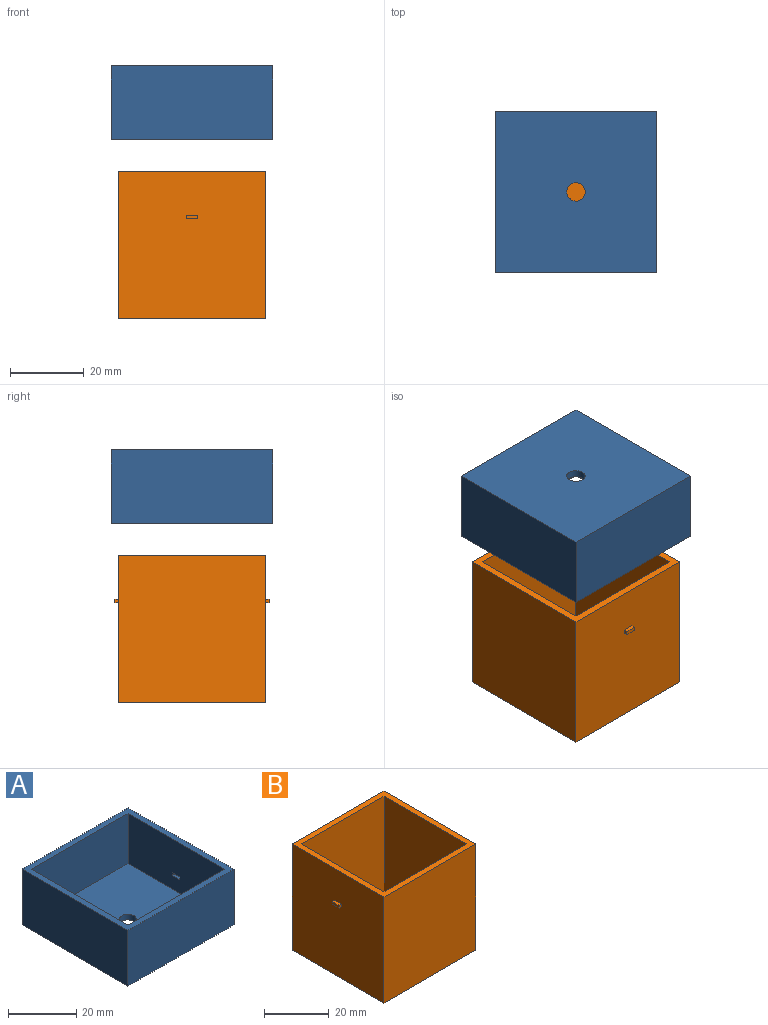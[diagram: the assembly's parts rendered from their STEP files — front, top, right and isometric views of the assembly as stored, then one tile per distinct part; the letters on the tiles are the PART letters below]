
ASSEMBLY  parts=2 mates=1
PART A: 22 faces, bbox 44x44x20 mm
  f0: plane 40x18mm, normal (1,0,0), area 717mm2, adj f2,f8,f9,f10,f17,f18,f19,f20
  f1: plane 40x18mm, normal (-1,0,0), area 717mm2, adj f2,f8,f9,f10,f12,f13,f14,f15
  f2: plane 44x44mm, normal (0,0,1), area 336mm2, adj f0,f1,f3,f4,f5,f6,f8,f9
  f3: plane 44x20mm, normal (0,1,0), area 880mm2, adj f2,f4,f6,f7
  f4: plane 44x20mm, normal (-1,0,0), area 880mm2, adj f2,f3,f5,f7
  f5: plane 44x20mm, normal (0,-1,0), area 880mm2, adj f2,f4,f6,f7
  f6: plane 44x20mm, normal (1,0,0), area 880mm2, adj f2,f3,f5,f7
  f7: plane 44x44mm, normal (0,0,-1), area 1916.4mm2, adj f3,f4,f5,f6,f11
  f8: plane 40x18mm, normal (0,-1,0), area 720mm2, adj f0,f1,f2,f10
  f9: plane 40x18mm, normal (0,1,0), area 720mm2, adj f0,f1,f2,f10
  f10: plane 40x40mm, normal (0,0,1), area 1580.4mm2, adj f0,f1,f8,f9,f11
  f11: cylinder r=2.5mm len=5mm, axis (0,0,-1), area 31.4mm2, adj f7,f10
  f12: plane 1x1mm, normal (0,-1,0), area 1mm2, adj f1,f13,f15,f16
  f13: plane 3x1mm, normal (0,0,1), area 3mm2, adj f1,f12,f14,f16
  f14: plane 1x1mm, normal (0,1,0), area 1mm2, adj f1,f13,f15,f16
  f15: plane 3x1mm, normal (0,0,-1), area 3mm2, adj f1,f12,f14,f16
  f16: plane 3x1mm, normal (-1,0,0), area 3mm2, adj f12,f13,f14,f15
  f17: plane 3x1mm, normal (0,0,1), area 3mm2, adj f0,f18,f20,f21
  f18: plane 1x1mm, normal (0,-1,0), area 1mm2, adj f0,f17,f19,f21
  f19: plane 3x1mm, normal (0,0,-1), area 3mm2, adj f0,f18,f20,f21
  f20: plane 1x1mm, normal (0,1,0), area 1mm2, adj f0,f17,f19,f21
  f21: plane 3x1mm, normal (1,0,0), area 3mm2, adj f17,f18,f19,f20
PART B: 21 faces, bbox 42x40x40 mm
  f0: plane 40x40mm, normal (1,0,0), area 1597mm2, adj f1,f2,f4,f5,f11,f12,f13,f14
  f1: plane 40x40mm, normal (0,0,1), area 304mm2, adj f0,f2,f3,f4,f6,f7,f8,f9
  f2: plane 40x40mm, normal (0,1,0), area 1600mm2, adj f0,f1,f3,f5
  f3: plane 40x40mm, normal (-1,0,0), area 1597mm2, adj f1,f2,f4,f5,f16,f17,f18,f19
  f4: plane 40x40mm, normal (0,-1,0), area 1600mm2, adj f0,f1,f3,f5
  f5: plane 40x40mm, normal (0,0,-1), area 1600mm2, adj f0,f2,f3,f4
  f6: plane 38x36mm, normal (0,-1,0), area 1368mm2, adj f1,f7,f9,f10
  f7: plane 38x36mm, normal (1,0,0), area 1368mm2, adj f1,f6,f8,f10
  f8: plane 38x36mm, normal (0,1,0), area 1368mm2, adj f1,f7,f9,f10
  f9: plane 38x36mm, normal (-1,0,0), area 1368mm2, adj f1,f6,f8,f10
  f10: plane 36x36mm, normal (0,0,1), area 1296mm2, adj f6,f7,f8,f9
  f11: plane 1x1mm, normal (0,-1,0), area 1mm2, adj f0,f12,f14,f15
  f12: plane 3x1mm, normal (0,0,-1), area 3mm2, adj f0,f11,f13,f15
  f13: plane 1x1mm, normal (0,1,0), area 1mm2, adj f0,f12,f14,f15
  f14: plane 3x1mm, normal (0,0,1), area 3mm2, adj f0,f11,f13,f15
  f15: plane 3x1mm, normal (1,0,0), area 3mm2, adj f11,f12,f13,f14
  f16: plane 1x1mm, normal (0,1,0), area 1mm2, adj f3,f17,f19,f20
  f17: plane 3x1mm, normal (0,0,-1), area 3mm2, adj f3,f16,f18,f20
  f18: plane 1x1mm, normal (0,-1,0), area 1mm2, adj f3,f17,f19,f20
  f19: plane 3x1mm, normal (0,0,1), area 3mm2, adj f3,f16,f18,f20
  f20: plane 3x1mm, normal (-1,0,0), area 3mm2, adj f16,f17,f18,f19
PLACE A rot(axis=(-1,0,0),180deg) t=(-49.22,-22.48,64.37)mm
PLACE B rot(axis=(0,0,-1),90deg) t=(-49.22,-22.48,-4.22)mm
MATE slider B.f10 <-> A.f11  axis (0,0,1) through (-49.22,-22.48,-2.22)mm
